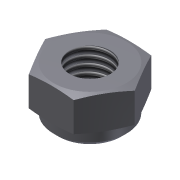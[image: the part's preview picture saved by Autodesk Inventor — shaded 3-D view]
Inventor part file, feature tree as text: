
AUTODESK INVENTOR PART (.ipt)
format: ipt  version: 2011 (Build 150239000, 239)  size: 104,960 bytes
history: native  units: in
note: dims shown in document units (in); Inventor stores cm internally (conversion verified against a paired STEP export)
features: other x1, imported_body x1, thread x1
ambient origin geometry x8: Origin, YZ Plane, XZ Plane, XY Plane, X Axis, Y Axis, Z Axis, Center Point
feature tree (3):
  other  "M5_Nylock-nut"
  imported_body  "Base1"
  thread  "Thread1"  [1 undecoded]
note: 1 required parameter value undecoded (feature->parameter linkage not recoverable at this tier; creation-order binding heuristic only, values carry confidence <= 0.55)
